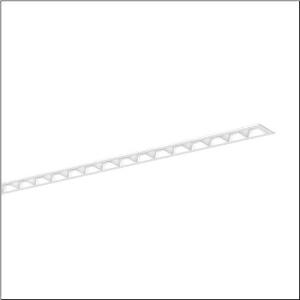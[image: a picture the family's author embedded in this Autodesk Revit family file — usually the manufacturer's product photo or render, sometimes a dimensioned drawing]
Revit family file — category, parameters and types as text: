
# Revit family: silica_r__21_51mx16db45wb_49d2
name_source: partatom
category: Lighting Fixtures
units: mm (PartAtom-declared; Revit-internal decimal feet)

## family parameters
Cut with Voids When Loaded = No
Host = Face
Light Source = No
Part Type = Normal
Room Calculation Point = No
Round Connector Dimension = Use Diameter
Shared = No

## types (1)
- --- (1 x LED, 5400 lm, 29.3 W, 4000K)
    Apparent Load = 29 VA
    CIE Flux Codes = 83 98 100 100 100
    Color Rendering = 80
    Color Temperature = 4000K
    Default Elevation = 1800 mm
    Description = Silica® 21, office luminaire, primary light control with darklight reflector, of PMMA, white, CAT 2 (L<= 3000cd/m²), light emission: direct distribution, primary light characteristic: symmetric, installation type: recessed, LED, rated luminous flux: 5.400lm, luminous efficacy: 184lm/W, light colour: 840, colour temperature: 4000K, with terminal, 3+2-pole, max. 2.5mm², mains connection: 220..240V, AC, 50/60Hz, rated input power: 29.3W, luminaire housing, of aluminium, traffic white (RAL 9016), length: 1.528mm, width: 79mm, height: 53mm, protection rating (complete): IP20, insulation class (complete): insulation class I (protective earthing), certification: CE, permissible operating ambient temperature: 0..+35°C, standard: EN 50419, packaging unit: 1 piece
    Height = 0 mm  [stored 0 ft]
    Lamp = 1 x LED
    Lamp Light Flux = 5400 lm
    Lamp Power = 29.3 W
    Lamp count = 1
    Length = 1527 mm
    Luminous efficacy = 184 lm/W
    Manufacturer = Siteco
    ModVariant = No
    Model = 51MX16DB45WB
    Mounting Place = Ceiling
    Mounting Type = Recessed
    Number of Poles = 1
    OnlyDefault = Yes
    Power Factor = 1
    Product Name = Silica® 21
    Product group = office luminaire | ceiling recessed
    ProductGroupID = 401
    Protection Class = Protection class I
    Protection Degree = IP 20
    RLX_Detail_Level = 1
    RLX_Emergency_Light_Flux = 0 lm
    RLX_Emergency_Type = 0
    RLX_Emergency_Type_DB = No
    RlxData = <blob elided: 39693 chars, md5=00ce8fe6>
    Socket = socket
    Standby Power = 0 W
    System Light Flux = 5400 lm
    System Power = 29 W
    Type Comments = factory setting: luminous flux: 100 % | dim-lin: 254 | 336 mA
    Type Image = l_1313606.jpg
    URL = http://relux.com
    VarID = @adj_073315
    Voltage = 0 V
    Weight = 0.00 kg
    Width = 79 mm

note: [stored X ft] marks values corroborated as IEEE doubles in the binary element streams (Revit-internal decimal feet)

## geometry (parser evidence)
native form markers: Blend x4, Sweep x10
no freeform markers — native parametric forms only
